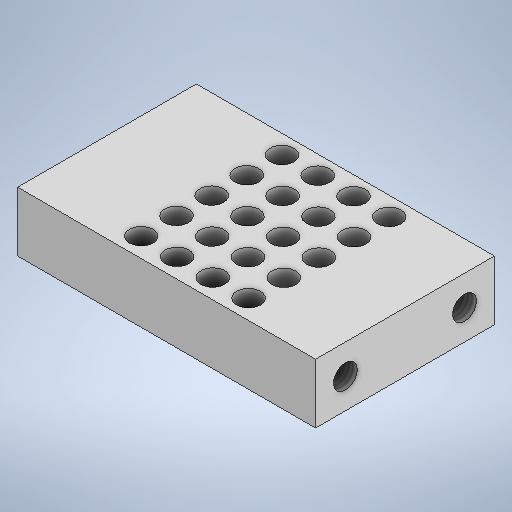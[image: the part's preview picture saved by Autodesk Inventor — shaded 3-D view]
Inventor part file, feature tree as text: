
AUTODESK INVENTOR PART (.ipt)
format: ipt  version: 2025.2 (Build 292293000, 293)  size: 321,024 bytes
history: native  units: mm
features: sketch x5, extrude x4, thread x4
ambient origin geometry x8: Origin, YZ Plane, XZ Plane, XY Plane, X Axis, Y Axis, Z Axis, Center Point
bodies: Solid1 (feature_tree)
feature tree (13):
  extrude  "Extrusion1"  Depth=30.0mm
  extrude  "Extrusion2"  Depth=10.0mm
  extrude  "Extrusion3"  Depth=10.0mm
  extrude  "Extrusion4"  Depth=10.0mm TaperAngle=0.0deg
  thread  "Thread1"  [1 undecoded]
  thread  "Thread2"  [1 undecoded]
  thread  "Thread3"  [1 undecoded]
  thread  "Thread4"  [1 undecoded]
  sketch  "Sketch1"  dims[d0=50.0mm d1=30.0mm]
  sketch  "Sketch2"  dims[d2=10.0mm d3=0.0mm d4=10.0mm]
  sketch  "Sketch3"  dims[d7=4.0mm d8=10.0mm d9=0.0mm d10=10.0mm d11=10.0mm d12=10.0mm d13=0.0mm d17=4.0mm]
  sketch  "Sketch4"  dims[d25=50.0mm d27=5.9mm d28=40.0mm d30=6.0mm d33=10.0mm d34=0.0mm d35=10.0mm d36=0.0mm d37=10.0mm d38=0.0mm d39=10.0mm d40=0.0mm d41=10.0mm d42=0.0mm]
  sketch  "Sketch Rectangular Pattern2"  dims[d5=10.0mm d6=4.0mm]
note: 4 required parameter values undecoded (feature->parameter linkage not recoverable at this tier; creation-order binding heuristic only, values carry confidence <= 0.55)
